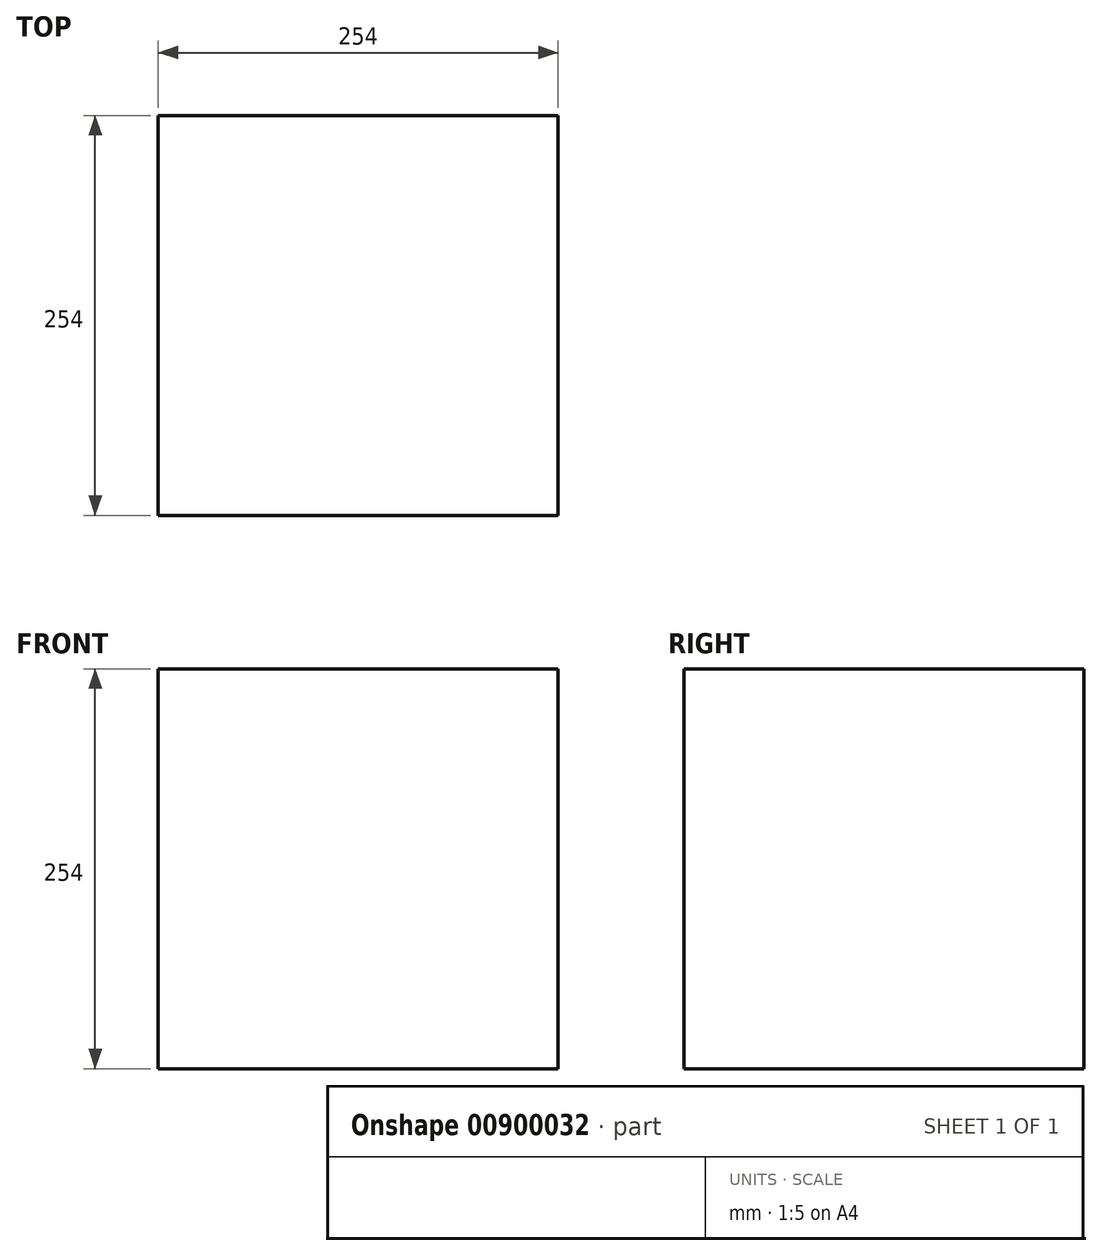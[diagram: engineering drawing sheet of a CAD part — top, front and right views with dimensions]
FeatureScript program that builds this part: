
annotation { "Feature Type Name" : "Feature", "Feature Type Description" : "" }
export const myFeature = defineFeature(function(context is Context, id is Id, definition is map)
    precondition{}
    {
        {
            var Q0;
            Q0=qCreatedBy(makeId("Front.planeOp"),FACE);
            var sketch = newSketch(context, id + "F0", { "sketchPlane" : qUnion([Q0])});
            skLineSegment(sketch, "E0.bottom", {"start": v(-136.3, 194.32) * mm, "end": v(117.7, 194.32) * mm});
            skLineSegment(sketch, "E0.top", {"start": v(-136.3, -59.68) * mm, "end": v(117.7, -59.68) * mm});
            skLineSegment(sketch, "E0.left", {"start": v(-136.3, 194.32) * mm, "end": v(-136.3, -59.68) * mm});
            skLineSegment(sketch, "E0.right", {"start": v(117.7, 194.32) * mm, "end": v(117.7, -59.68) * mm});
            skSolve(sketch);
        }
        {
            var Q0;
            Q0 = qSketchRegion(id + "F0", true);
            extrude(context, id + "F1", {"entities" : qUnion([Q0]), "depth" : 254 * mm, "offsetDistance" : 25.4 * mm});
        }
    });
